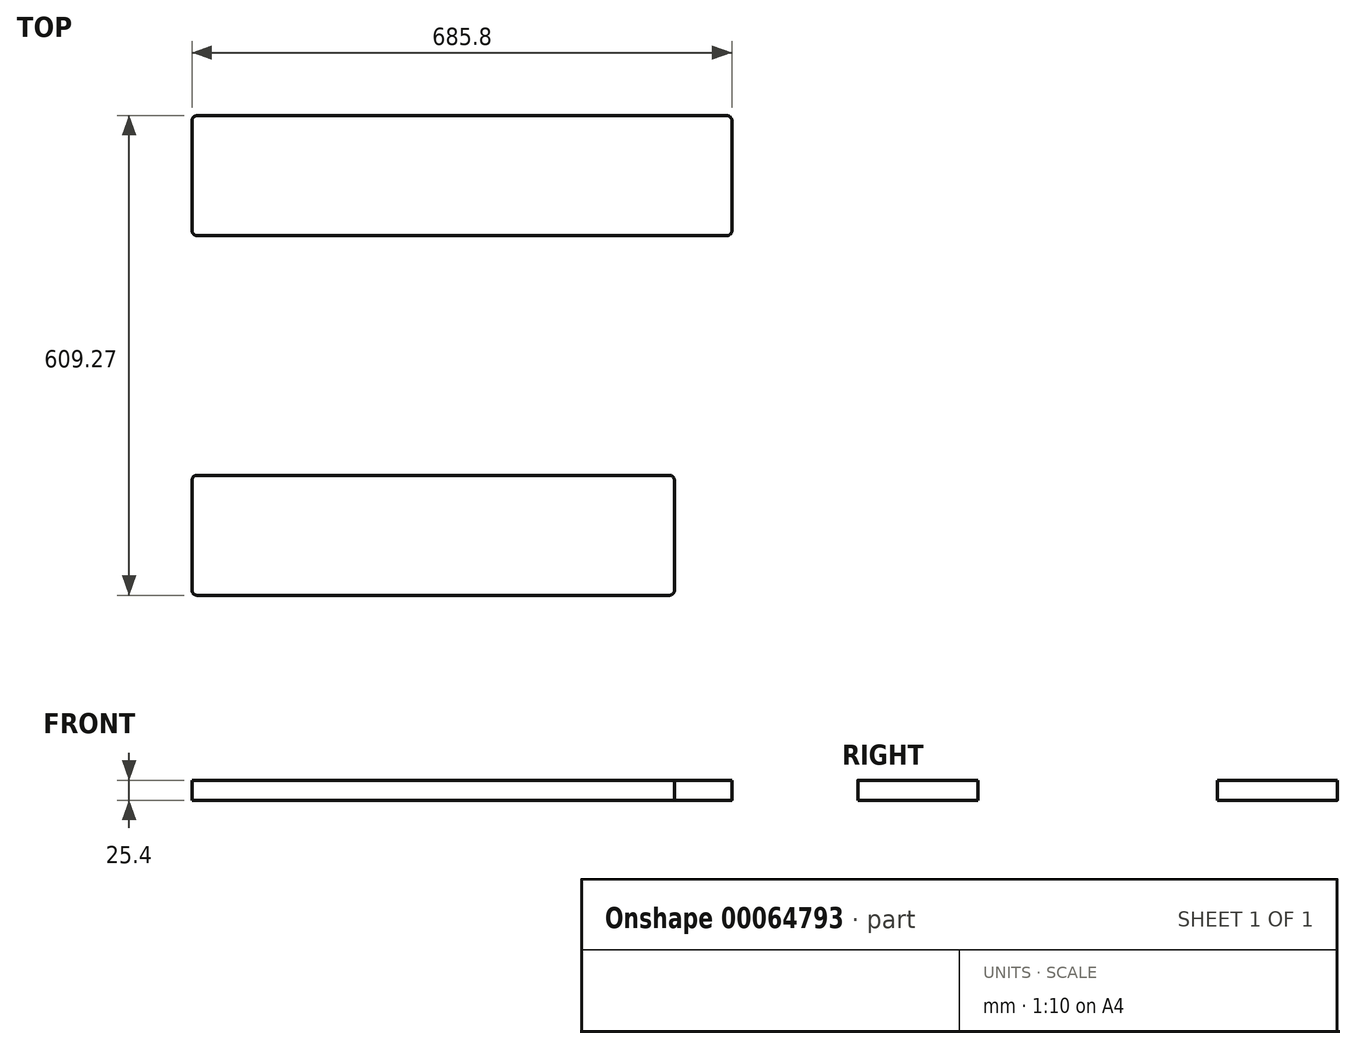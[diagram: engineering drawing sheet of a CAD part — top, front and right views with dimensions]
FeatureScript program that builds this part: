
annotation { "Feature Type Name" : "Feature", "Feature Type Description" : "" }
export const myFeature = defineFeature(function(context is Context, id is Id, definition is map)
    precondition{}
    {
        {
            var Q0;
            Q0=qCreatedBy(makeId("Top.planeOp"),FACE);
            var sketch = newSketch(context, id + "F0", { "sketchPlane" : qUnion([Q0])});
            skLineSegment(sketch, "E0.bottom", {"start": v(0, 0) * mm, "end": v(685.8, 0) * mm});
            skLineSegment(sketch, "E0.top", {"start": v(0, 152.4) * mm, "end": v(685.8, 152.4) * mm});
            skLineSegment(sketch, "E0.left", {"start": v(0, 0) * mm, "end": v(0, 152.4) * mm});
            skLineSegment(sketch, "E0.right", {"start": v(685.8, 0) * mm, "end": v(685.8, 152.4) * mm});
            skLineSegment(sketch, "E1.bottom", {"start": v(0, -304.47) * mm, "end": v(612.78, -304.47) * mm});
            skLineSegment(sketch, "E1.top", {"start": v(0, -456.87) * mm, "end": v(612.78, -456.87) * mm});
            skLineSegment(sketch, "E1.left", {"start": v(0, -304.47) * mm, "end": v(0, -456.87) * mm});
            skLineSegment(sketch, "E1.right", {"start": v(612.78, -304.47) * mm, "end": v(612.78, -456.87) * mm});
            skSolve(sketch);
        }
        {
            var Q0;
            Q0 = qSketchRegion(id + "F0", true);
            extrude(context, id + "F1", {"entities" : qUnion([Q0]), "depth" : 25.4 * mm});
        }
        {
            var Q0;
            Q0=makeQuery(id+"F1.opExtrude","SWEPT_EDGE",EDGE,{"disambiguationData":[OSD([sQuery(id+"F0.wireOp",EDGE,"E0.top"),sQuery(id+"F0.wireOp",EDGE,"E0.left")])]});
            var Q1;
            Q1=makeQuery(id+"F1.opExtrude","SWEPT_EDGE",EDGE,{"disambiguationData":[OSD([sQuery(id+"F0.wireOp",EDGE,"E0.bottom"),sQuery(id+"F0.wireOp",EDGE,"E0.left")])]});
            var Q2;
            Q2=makeQuery(id+"F1.opExtrude","SWEPT_EDGE",EDGE,{"disambiguationData":[OSD([sQuery(id+"F0.wireOp",EDGE,"E0.bottom"),sQuery(id+"F0.wireOp",EDGE,"E0.right")])]});
            var Q3;
            Q3=makeQuery(id+"F1.opExtrude","SWEPT_EDGE",EDGE,{"disambiguationData":[OSD([sQuery(id+"F0.wireOp",EDGE,"E0.top"),sQuery(id+"F0.wireOp",EDGE,"E0.right")])]});
            var Q4;
            Q4=makeQuery(id+"F1.opExtrude","SWEPT_EDGE",EDGE,{"disambiguationData":[OSD([sQuery(id+"F0.wireOp",EDGE,"E1.top"),sQuery(id+"F0.wireOp",EDGE,"E1.right")])]});
            var Q5;
            Q5=makeQuery(id+"F1.opExtrude","SWEPT_EDGE",EDGE,{"disambiguationData":[OSD([sQuery(id+"F0.wireOp",EDGE,"E1.top"),sQuery(id+"F0.wireOp",EDGE,"E1.left")])]});
            var Q6;
            Q6=makeQuery(id+"F1.opExtrude","SWEPT_EDGE",EDGE,{"disambiguationData":[OSD([sQuery(id+"F0.wireOp",EDGE,"E1.bottom"),sQuery(id+"F0.wireOp",EDGE,"E1.left")])]});
            var Q7;
            Q7=makeQuery(id+"F1.opExtrude","SWEPT_EDGE",EDGE,{"disambiguationData":[OSD([sQuery(id+"F0.wireOp",EDGE,"E1.bottom"),sQuery(id+"F0.wireOp",EDGE,"E1.right")])]});
            fillet(context, id + "F2", {"entities" : qUnion([Q0, Q1, Q2, Q3, Q4, Q5, Q6, Q7]), "radius" : 6.35 * mm, "tangentPropagation" : true, "allowEdgeOverflow" : false});
        }
    });
